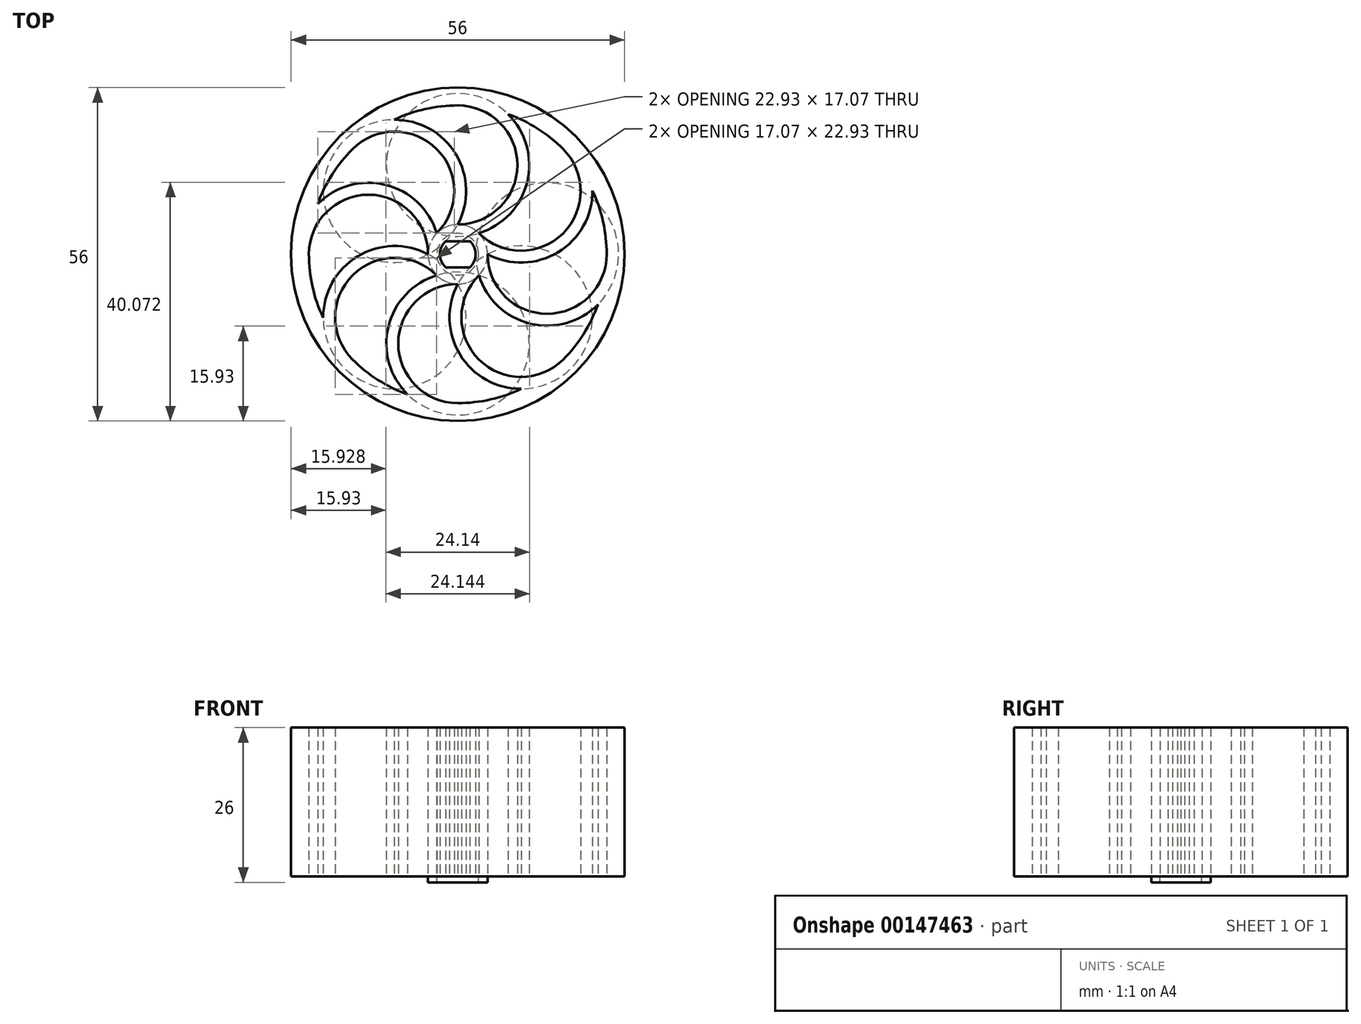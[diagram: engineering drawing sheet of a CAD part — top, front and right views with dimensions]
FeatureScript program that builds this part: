
annotation { "Feature Type Name" : "Feature", "Feature Type Description" : "" }
export const myFeature = defineFeature(function(context is Context, id is Id, definition is map)
    precondition{}
    {
        {
            var Q0;
            Q0=qCreatedBy(makeId("Top.planeOp"),FACE);
            var sketch = newSketch(context, id + "F0", { "sketchPlane" : qUnion([Q0])});
            skCircle(sketch, "E0", {"center": v(0, 0) * mm, "radius": 28 * mm});
            skCircle(sketch, "E1", {"center": v(0, 0) * mm, "radius": 25 * mm});
            skArc(sketch, "E2", {"start": v(-5, 0) * mm, "mid": v(-5, 0) * mm, "end": v(-5, 0) * mm});
            skPoint(sketch, "E3", {"position": v(0, 25) * mm});
            skPoint(sketch, "E4", {"position": v(-25, 0) * mm});
            skPoint(sketch, "E5", {"position": v(25, 0) * mm});
            skPoint(sketch, "E6", {"position": v(0, -25) * mm});
            skPoint(sketch, "E7", {"position": v(-5, 0) * mm});
            skPoint(sketch, "E8", {"position": v(-3.54, 3.54) * mm});
            skPoint(sketch, "E9", {"position": v(-17.68, -17.68) * mm});
            skPoint(sketch, "E10", {"position": v(17.68, -17.68) * mm});
            skPoint(sketch, "E11", {"position": v(17.68, 17.68) * mm});
            skPoint(sketch, "E12", {"position": v(-17.68, 17.68) * mm});
            skArc(sketch, "E13", {"start": v(-5, 0) * mm, "mid": v(-15, 10) * mm, "end": v(-25, 0) * mm});
            skArc(sketch, "E14.trimOffspring", {"start": v(-3.53, 3.54) * mm, "mid": v(-16.79, 11.87) * mm, "end": v(-27, 0) * mm});
            skArc(sketch, "E15.1.0", {"start": v(-3.54, -3.54) * mm, "mid": v(-17.68, -3.54) * mm, "end": v(-17.68, -17.68) * mm});
            skArc(sketch, "E15.1.1", {"start": v(-5, 0) * mm, "mid": v(-20.26, -3.48) * mm, "end": v(-19.1, -19.1) * mm});
            skArc(sketch, "E15.2.0", {"start": v(0, -5) * mm, "mid": v(-10, -15) * mm, "end": v(0, -25) * mm});
            skArc(sketch, "E15.2.1", {"start": v(-3.54, -3.53) * mm, "mid": v(-11.87, -16.79) * mm, "end": v(0, -27) * mm});
            skArc(sketch, "E15.3.0", {"start": v(3.54, -3.54) * mm, "mid": v(3.54, -17.68) * mm, "end": v(17.68, -17.68) * mm});
            skArc(sketch, "E15.3.1", {"start": v(0, -5) * mm, "mid": v(3.48, -20.26) * mm, "end": v(19.1, -19.1) * mm});
            skArc(sketch, "E15.4.0", {"start": v(5, 0) * mm, "mid": v(15, -10) * mm, "end": v(25, 0) * mm});
            skArc(sketch, "E15.4.1", {"start": v(3.53, -3.54) * mm, "mid": v(16.79, -11.87) * mm, "end": v(27, 0) * mm});
            skArc(sketch, "E15.5.0", {"start": v(3.54, 3.54) * mm, "mid": v(17.68, 3.54) * mm, "end": v(17.68, 17.68) * mm});
            skArc(sketch, "E15.5.1", {"start": v(5, 0) * mm, "mid": v(20.26, 3.48) * mm, "end": v(19.1, 19.1) * mm});
            skArc(sketch, "E15.6.0", {"start": v(0, 5) * mm, "mid": v(10, 15) * mm, "end": v(0, 25) * mm});
            skArc(sketch, "E15.6.1", {"start": v(3.54, 3.53) * mm, "mid": v(11.87, 16.79) * mm, "end": v(0, 27) * mm});
            skArc(sketch, "E15.7.0", {"start": v(-3.54, 3.54) * mm, "mid": v(-3.54, 17.68) * mm, "end": v(-17.68, 17.68) * mm});
            skArc(sketch, "E15.7.1", {"start": v(0, 5) * mm, "mid": v(-3.48, 20.26) * mm, "end": v(-19.1, 19.1) * mm});
            skSolve(sketch);
        }
        {
            var Q0;
            {var subQ1=sQuery(id+"F0.wireOp",EDGE,"E15.5.0");var subQ3=sQuery(id+"F0.wireOp",EDGE,"E1");var subQ40=makeQuery(id+"F0.imprint","INTERSECT",VERTEX,{"derivedFrom":[subQ3,subQ1]});Q0=makeQuery(id+"F0.imprint","IMPRINT",FACE,{"disambiguationData":[TD([[makeQuery(id+"F0.imprint","IMPRINT",EDGE,{"disambiguationData":[TD([[subQ40,1.0]])],"derivedFrom":subQ3}),1.0]])]});}
            var Q1;
            Q1=makeQuery(id+"F0.imprint","IMPRINT",FACE,{"disambiguationData":[TD([[makeQuery(id+"F0.imprint","IMPRINT",EDGE,{"derivedFrom":sQuery(id+"F0.wireOp",EDGE,"E0")}),1.0]])]});
            extrude(context, id + "F1", {"entities" : qUnion([Q0, Q1]), "depth" : 25 * mm});
        }
        {
            var Q0;
            Q0=qCreatedBy(makeId("Top.planeOp"),FACE);
            var sketch = newSketch(context, id + "F2", { "sketchPlane" : qUnion([Q0])});
            skCircle(sketch, "E16", {"center": v(0, 0) * mm, "radius": 3 * mm});
            skLineSegment(sketch, "E17.bottom", {"start": v(-2.04, -2.2) * mm, "end": v(2.04, -2.2) * mm});
            skLineSegment(sketch, "E17.top", {"start": v(-2.04, 2.2) * mm, "end": v(2.04, 2.2) * mm});
            skLineSegment(sketch, "E17.left", {"start": v(-2.04, -2.2) * mm, "end": v(-2.04, 2.2) * mm});
            skLineSegment(sketch, "E17.right", {"start": v(2.04, -2.2) * mm, "end": v(2.04, 2.2) * mm});
            skSolve(sketch);
        }
        {
            var Q0;
            {var subQ0=sQuery(id+"F2.wireOp",EDGE,"E17.left");Q0=makeQuery(id+"F2.imprint","IMPRINT",FACE,{"disambiguationData":[TD([[makeQuery(id+"F2.imprint","IMPRINT",EDGE,{"derivedFrom":subQ0}),1.0]])]});}
            var Q1;
            Q1=makeQuery(id+"F2.imprint","IMPRINT",FACE,{"disambiguationData":[TD([[makeQuery(id+"F2.imprint","IMPRINT",EDGE,{"derivedFrom":sQuery(id+"F2.wireOp",EDGE,"E17.bottom")}),1.0]])]});
            var Q2;
            {var subQ0=sQuery(id+"F2.wireOp",EDGE,"E17.right");Q2=makeQuery(id+"F2.imprint","IMPRINT",FACE,{"disambiguationData":[TD([[makeQuery(id+"F2.imprint","IMPRINT",EDGE,{"derivedFrom":subQ0}),-1.0]])]});}
            extrude(context, id + "F3", {"entities" : qUnion([Q0, Q1, Q2]), "operationType" : NewBodyOperationType.REMOVE, "depth" : 30 * mm});
        }
        {
            var Q0;
            Q0=qCreatedBy(makeId("Top.planeOp"),FACE);
            var sketch = newSketch(context, id + "F4", { "sketchPlane" : qUnion([Q0])});
            skCircle(sketch, "E18", {"center": v(0, 0) * mm, "radius": 5 * mm});
            skCircle(sketch, "E19", {"center": v(0, 0) * mm, "radius": 3.5 * mm});
            skSolve(sketch);
        }
        {
            var Q0;
            Q0 = qSketchRegion(id + "F4", true);
            extrude(context, id + "F5", {"entities" : qUnion([Q0]), "operationType" : NewBodyOperationType.ADD, "oppositeDirection" : true, "depth" : 1 * mm});
        }
    });
